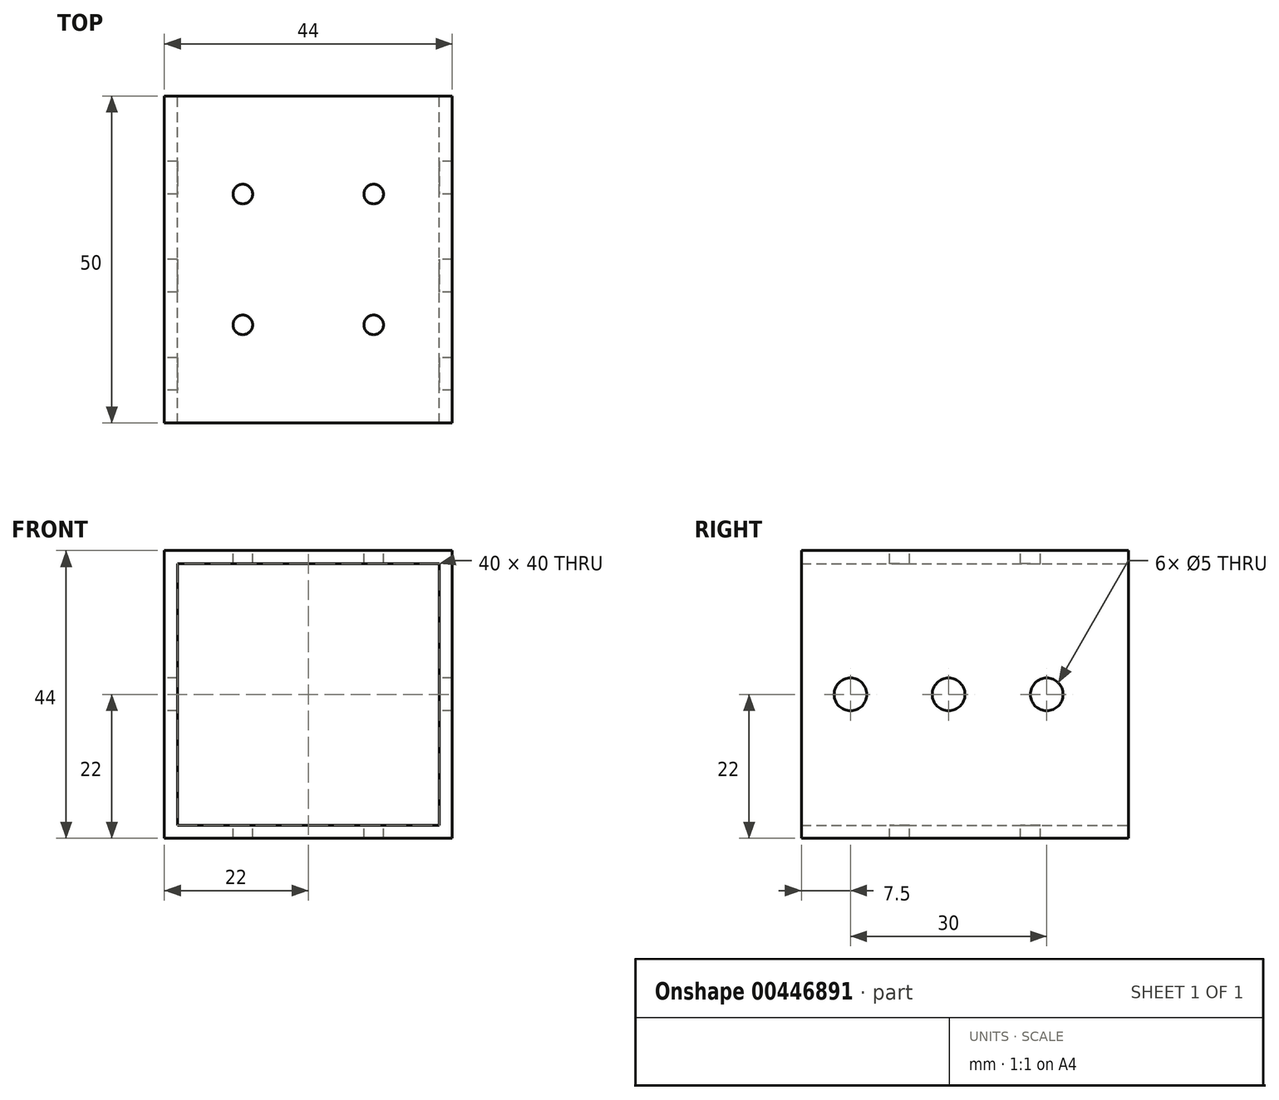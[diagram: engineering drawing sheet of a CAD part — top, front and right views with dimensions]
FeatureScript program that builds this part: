
annotation { "Feature Type Name" : "Feature", "Feature Type Description" : "" }
export const myFeature = defineFeature(function(context is Context, id is Id, definition is map)
    precondition{}
    {
        {
            var Q0;
            Q0=qCreatedBy(makeId("Front.planeOp"),FACE);
            var sketch = newSketch(context, id + "F0", { "sketchPlane" : qUnion([Q0])});
            skLineSegment(sketch, "E0.bottom", {"start": v(20, -20) * mm, "end": v(-20, -20) * mm});
            skLineSegment(sketch, "E0.top", {"start": v(20, 20) * mm, "end": v(-20, 20) * mm});
            skLineSegment(sketch, "E0.left", {"start": v(20, -20) * mm, "end": v(20, 20) * mm});
            skLineSegment(sketch, "E0.right", {"start": v(-20, -20) * mm, "end": v(-20, 20) * mm});
            skPoint(sketch, "E0.middle", {"position": v(0, 0) * mm});
            skLineSegment(sketch, "E1.0", {"start": v(22, 22) * mm, "end": v(-22, 22) * mm});
            skLineSegment(sketch, "E1.1", {"start": v(22, -22) * mm, "end": v(22, 22) * mm});
            skLineSegment(sketch, "E1.2", {"start": v(22, -22) * mm, "end": v(-22, -22) * mm});
            skLineSegment(sketch, "E1.3", {"start": v(-22, -22) * mm, "end": v(-22, 22) * mm});
            skSolve(sketch);
        }
        {
            var Q0;
            Q0=makeQuery(id+"F0.imprint","IMPRINT",FACE,{"disambiguationData":[TD([[makeQuery(id+"F0.imprint","IMPRINT",EDGE,{"derivedFrom":sQuery(id+"F0.wireOp",EDGE,"E0.bottom")}),1.0]])]});
            extrude(context, id + "F1", {"entities" : qUnion([Q0]), "depth" : 50 * mm});
        }
        {
            var Q0;
            Q0=makeQuery(id+"F1.opExtrude","SWEPT_FACE",FACE,{"disambiguationData":[OSD([sQuery(id+"F0.wireOp",EDGE,"E1.0")])]});
            var sketch = newSketch(context, id + "F2", { "sketchPlane" : qUnion([Q0])});
            skLineSegment(sketch, "E2", {"start": v(0, 0) * mm, "end": v(0, -50) * mm, "construction": true});
            skLineSegment(sketch, "E3.bottom", {"start": v(-10, -35) * mm, "end": v(10, -35) * mm, "construction": true});
            skLineSegment(sketch, "E3.top", {"start": v(-10, -15) * mm, "end": v(10, -15) * mm, "construction": true});
            skLineSegment(sketch, "E3.left", {"start": v(-10, -35) * mm, "end": v(-10, -15) * mm, "construction": true});
            skLineSegment(sketch, "E3.right", {"start": v(10, -35) * mm, "end": v(10, -15) * mm, "construction": true});
            skPoint(sketch, "E3.middle", {"position": v(0, -25) * mm});
            skCircle(sketch, "E4", {"center": v(10, -15) * mm, "radius": 1.5 * mm});
            skCircle(sketch, "E5", {"center": v(10, -35) * mm, "radius": 1.5 * mm});
            skCircle(sketch, "E6", {"center": v(-10, -35) * mm, "radius": 1.5 * mm});
            skCircle(sketch, "E7", {"center": v(-10, -15) * mm, "radius": 1.5 * mm});
            skSolve(sketch);
        }
        {
            var Q0;
            Q0=makeQuery(id+"F2.imprint","IMPRINT",FACE,{"disambiguationData":[TD([[makeQuery(id+"F2.imprint","IMPRINT",EDGE,{"derivedFrom":sQuery(id+"F2.wireOp",EDGE,"E4")}),1.0]])]});
            var Q1;
            Q1=makeQuery(id+"F2.imprint","IMPRINT",FACE,{"disambiguationData":[TD([[makeQuery(id+"F2.imprint","IMPRINT",EDGE,{"derivedFrom":sQuery(id+"F2.wireOp",EDGE,"E5")}),1.0]])]});
            var Q2;
            Q2=makeQuery(id+"F2.imprint","IMPRINT",FACE,{"disambiguationData":[TD([[makeQuery(id+"F2.imprint","IMPRINT",EDGE,{"derivedFrom":sQuery(id+"F2.wireOp",EDGE,"E6")}),1.0]])]});
            var Q3;
            Q3=makeQuery(id+"F2.imprint","IMPRINT",FACE,{"disambiguationData":[TD([[makeQuery(id+"F2.imprint","IMPRINT",EDGE,{"derivedFrom":sQuery(id+"F2.wireOp",EDGE,"E7")}),1.0]])]});
            extrude(context, id + "F3", {"entities" : qUnion([Q0, Q1, Q2, Q3]), "operationType" : NewBodyOperationType.REMOVE, "endBound" : BoundingType.THROUGH_ALL, "oppositeDirection" : true, "depth" : 25 * mm});
        }
        {
            var Q0;
            Q0=makeQuery(id+"F1.opExtrude","SWEPT_FACE",FACE,{"disambiguationData":[OSD([sQuery(id+"F0.wireOp",EDGE,"E1.3")])]});
            var sketch = newSketch(context, id + "F4", { "sketchPlane" : qUnion([Q0])});
            skLineSegment(sketch, "E8", {"start": v(0, 0) * mm, "end": v(50, 0) * mm, "construction": true});
            skCircle(sketch, "E9", {"center": v(12.5, 0) * mm, "radius": 2.5 * mm});
            skCircle(sketch, "E10", {"center": v(27.5, 0) * mm, "radius": 2.5 * mm});
            skCircle(sketch, "E11", {"center": v(42.5, 0) * mm, "radius": 2.5 * mm});
            skSolve(sketch);
        }
        {
            var Q0;
            Q0=makeQuery(id+"F4.imprint","IMPRINT",FACE,{"disambiguationData":[TD([[makeQuery(id+"F4.imprint","IMPRINT",EDGE,{"derivedFrom":sQuery(id+"F4.wireOp",EDGE,"E9")}),1.0]])]});
            var Q1;
            Q1=makeQuery(id+"F4.imprint","IMPRINT",FACE,{"disambiguationData":[TD([[makeQuery(id+"F4.imprint","IMPRINT",EDGE,{"derivedFrom":sQuery(id+"F4.wireOp",EDGE,"E10")}),1.0]])]});
            var Q2;
            Q2=makeQuery(id+"F4.imprint","IMPRINT",FACE,{"disambiguationData":[TD([[makeQuery(id+"F4.imprint","IMPRINT",EDGE,{"derivedFrom":sQuery(id+"F4.wireOp",EDGE,"E11")}),1.0]])]});
            extrude(context, id + "F5", {"entities" : qUnion([Q0, Q1, Q2]), "operationType" : NewBodyOperationType.REMOVE, "endBound" : BoundingType.THROUGH_ALL, "oppositeDirection" : true, "depth" : 25 * mm});
        }
    });
